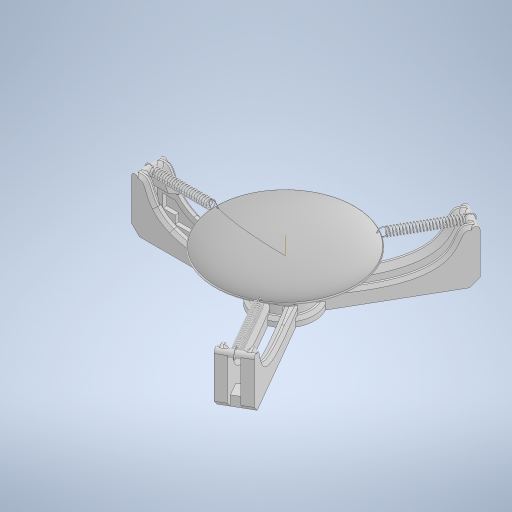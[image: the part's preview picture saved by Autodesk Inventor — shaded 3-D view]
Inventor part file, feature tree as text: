
AUTODESK INVENTOR PART (.ipt)
format: ipt  version: 2024.1 (Build 281209000, 209)  size: 2,369,024 bytes
history: native  units: mm
features: sketch x22, projected_geometry x21, extrude x18, fillet x5, chamfer x5, pattern_circular x4, other x3, mirror x2, revolve x1, helix x1, plane x1, imported_body x1
ambient origin geometry x8: Origin, YZ Plane, XZ Plane, XY Plane, X Axis, Y Axis, Z Axis, Center Point
bodies: Body1 (feature_tree), Body2 (feature_tree), Body3 (feature_tree), Body4 (feature_tree)
feature tree (84):
  other  "dish"
  revolve  "Revolution1"  [1 undecoded]
  extrude  "Extrusion2"  Depth=0.5mm
  pattern_circular  "Circular Pattern1"  Count=3 Angle=360.0deg
  extrude  "Extrusion3"  Depth=0.9mm
  fillet  "Fillet2"  Radius=73.4mm
  helix  "Coil1"  [1 undecoded]
  extrude  "Extrusion4"  Depth=1.2mm
  fillet  "Fillet3"  Radius=4.127824mm
  extrude  "Extrusion5"  Depth=65.0mm
  fillet  "Fillet4"  Radius=1.0mm
  fillet  "Fillet5"  Radius=0.45mm
  pattern_circular  "Circular Pattern2"  Count=3 Angle=360.0deg
  extrude  "Extrusion6"  Depth=10.0mm TaperAngle=0.0deg
  extrude  "Extrusion7"  Depth=15.0mm
  mirror  "Mirror1"
  pattern_circular  "Circular Pattern3"  Count=3 Angle=360.0deg
  extrude  "Extrusion10"  Depth=25.0mm
  pattern_circular  "Circular Pattern4"  Count=4  [1 undecoded]
  extrude  "Extrusion11"  Depth=12.5mm
  extrude  "Extrusion12"  Depth=2.5mm TaperAngle=0.0deg
  extrude  "Extrusion13"  Depth=2.5mm
  sketch  "Sketch16"  dims[d40=0.45mm]
  chamfer  "Chamfer1"  Distance=2.5mm
  extrude  "Extrusion14"  Depth=3.0mm
  chamfer  "Chamfer2"  Distance=8.0mm
  fillet  "Fillet6"  Radius=8.0mm
  extrude  "Extrusion15"  Depth=3.0mm TaperAngle=0.0deg
  plane  "Work Plane1"
  mirror  "Mirror2"
  sketch  "Sketch20"  dims[d49=30.0mm d50=360.0deg d57=15.0mm]
  extrude  "Extrusion17"  Depth=3.0mm TaperAngle=45.0deg
  extrude  "Extrusion18"  Depth=3.0mm
  extrude  "Extrusion19"  Depth=3.0mm TaperAngle=0.0deg
  extrude  "Extrusion20"  TaperAngle=60.0deg  [1 undecoded]
  extrude  "Extrusion21"  Depth=3.0mm
  chamfer  "Chamfer3"  Distance=0.1mm
  extrude  "Extrusion22"  Depth=3.0mm
  chamfer  "Chamfer4"  Distance=0.1mm
  chamfer  "Chamfer5"  Distance=0.1mm
  sketch  "Sketch2"  dims[d4=70.5mm d5=1.9mm]
  sketch  "Sketch3"  dims[d6=8.0mm d7=0.5mm]
  sketch  "Sketch4"  dims[d8=0.95mm]
  projected_geometry  "Projected Loop1"
  other  "spring"
  sketch  "Sketch5"  dims[d9=90.0deg]
  sketch  "Sketch6"  dims[d10=1.5mm]
  sketch  "Sketch7"  dims[d11=69.0mm]
  sketch  "Sketch8"  dims[d12=0.0mm d13=0.0mm d14=30.0mm d15=360.0deg]
  sketch  "Sketch9"  dims[d17=9.65mm d18=0.9mm d19=73.4mm d20=1.0mm d21=0.0mm]
  imported_body  "base"
  sketch  "Sketch12"  dims[d22=0.45mm d23=1.2mm d24=4.127824mm]
  sketch  "Sketch13"  dims[d25=75.104637mm]
  sketch  "Sketch14"  dims[d26=2.3mm d27=60.0mm d28=240.0mm d29=0.0mm d30=90.0deg d31=90.0deg d32=0.0mm d33=0.0mm d34=65.0mm d35=1.0mm d36=0.0mm d37=0.45mm]
  projected_geometry  "Projected Loop2"
  projected_geometry  "Projected Loop3"
  sketch  "Sketch15"  dims[d38=0.0mm d39=0.0mm]
  sketch  "Sketch17"  dims[d41=3.0mm d42=30.0mm d43=360.0deg]
  sketch  "Sketch18"  dims[d45=10.0mm d46=0.0mm d47=10.0mm d48=0.0mm]
  projected_geometry  "Projected Loop4"
  sketch  "Sketch21"  dims[d58=10.0mm d59=0.0mm d60=30.0mm d61=360.0deg]
  projected_geometry  "Projected Loop6"
  sketch  "Sketch22"  dims[d63=25.0mm d66=25.0mm d67=40.0mm d68=0.0mm]
  projected_geometry  "Projected Loop7"
  projected_geometry  "Projected Loop8"
  projected_geometry  "Projected Loop9"
  other  "lock"
  sketch  "Sketch23"  dims[d69=12.5mm d70=12.5mm]
  sketch  "Sketch25"  dims[d71=10.9mm d72=2.5mm d73=0.0mm]
  sketch  "Sketch26"  dims[d74=25.0mm d75=2.5mm]
  projected_geometry  "Projected Loop28"
  projected_geometry  "Projected Loop29"
  projected_geometry  "Projected Loop30"
  projected_geometry  "Projected Loop31"
  projected_geometry  "Projected Loop32"
  projected_geometry  "Projected Loop33"
  projected_geometry  "Projected Loop34"
  projected_geometry  "Projected Loop35"
  projected_geometry  "Projected Loop36"
  sketch  "Sketch27"  dims[d77=50.0mm d78=2.5mm d79=0.0mm d81=2.5mm d82=8.0mm d83=8.0mm d84=2.0mm d85=45.0deg d86=4.75mm d87=0.0mm d88=5.0mm d89=2.0mm d90=45.0deg d91=5.0mm d92=4.0mm d93=0.0mm d95=60.0deg d115=8.0mm d116=0.1mm d118=0.1mm d119=0.1mm d120=0.1mm d121=0.1mm d122=0.1mm d123=0.0mm d124=0.0mm d125=50.0mm d126=0.01mm d127=0.01mm d128=0.01mm d129=10.0mm d130=0.0mm d131=8.0mm d132=0.0mm d133=60.0mm d134=3.0mm d135=0.0mm d136=15.0mm d137=0.0mm d138=2.0mm d139=2.0mm d140=45.0deg d141=0.01mm d142=0.01mm d143=0.01mm d144=0.01mm d145=0.01mm d146=0.5mm d147=0.0mm d148=3.0mm d149=2.0mm d150=45.0deg d151=3.0mm d152=2.0mm d153=45.0deg]
  projected_geometry  "Projected Loop37"
  projected_geometry  "Projected Loop38"
  projected_geometry  "Projected Loop39"
  projected_geometry  "Projected Loop40"
note: 4 required parameter values undecoded (feature->parameter linkage not recoverable at this tier; creation-order binding heuristic only, values carry confidence <= 0.55)